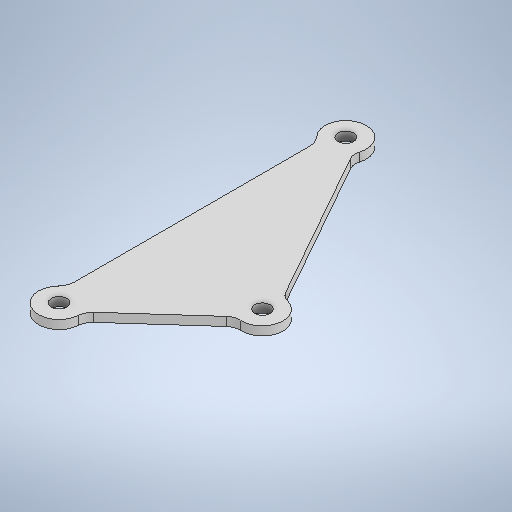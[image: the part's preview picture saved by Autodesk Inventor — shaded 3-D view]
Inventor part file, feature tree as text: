
AUTODESK INVENTOR PART (.ipt)
format: ipt  version: 2025.2 (Build 292293000, 293)  size: 312,832 bytes
history: native  units: in
note: dims shown in document units (in); Inventor stores cm internally (conversion verified against a paired STEP export)
features: extrude x4, sketch x3
ambient origin geometry x8: Origin, YZ Plane, XZ Plane, XY Plane, X Axis, Y Axis, Z Axis, Center Point
bodies: Solid1 (feature_tree)
feature tree (7):
  sketch  "Sketch1"  dims[d0=0.315in d1=0.315in]
  extrude  "Extrusion1"  Depth=0.315in
  extrude  "Extrusion2"  Depth=1.6732in
  extrude  "Extrusion3"  Depth=2.1946in
  extrude  "Extrusion4"  Depth=2.1946in
  sketch  "Sketch2"  dims[d2=0.315in d4=1.6732in]
  sketch  "Sketch3"  dims[d5=1.1024in d6=0.0787in d7=0.0787in d8=0.1969in d10=0.1969in d11=0.0in d12=0.2066in d14=0.2066in d15=0.0787in d16=0.0787in d17=0.0787in d18=0.0787in d19=0.1575in d20=0.1969in d21=0.1969in d22=0.1969in d23=0.0433in d24=0.0521in d25=0.1575in d26=0.0in d27=0.0669in d28=0.0in d29=0.1181in d30=0.1181in d31=0.1181in d32=0.1575in d33=0.0in d34=3.937in d35=0.0in d36=0.0in d38=2.1946in]
